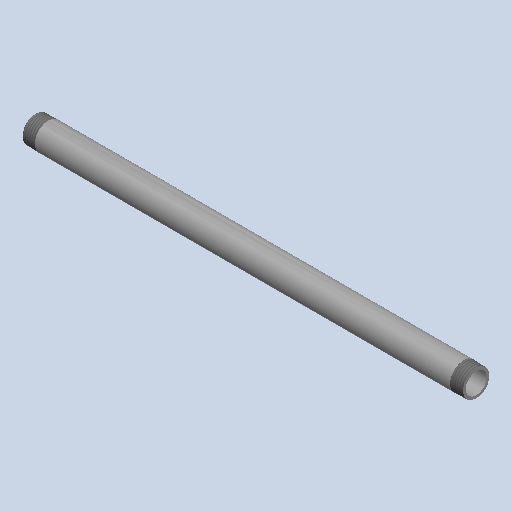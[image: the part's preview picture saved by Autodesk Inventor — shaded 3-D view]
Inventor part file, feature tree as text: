
AUTODESK INVENTOR PART (.ipt)
format: ipt  version: 2025 (Build 290162000, 162)  size: 181,760 bytes
history: native  units: mm (DEFAULTED — no unit token found)
features: other x8, revolve x1
ambient origin geometry x8: Origin, YZ Plane, XZ Plane, XY Plane, X Axis, Y Axis, Z Axis, Center Point
bodies: Solid1 (feature_tree)
feature tree (9):
  revolve  "Revolution1"  [1 undecoded]
  other  "Work Axis1"
  other  "Work Point5"
  other  "Work Axis2"
  other  "Work Point6"
  other  "Work Axis3"
  other  "Work Axis4"
  other  "Work Point7"
  other  "Work Point8"
note: 1 required parameter value undecoded (feature->parameter linkage not recoverable at this tier; creation-order binding heuristic only, values carry confidence <= 0.55)
